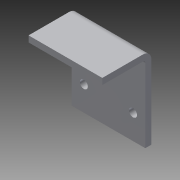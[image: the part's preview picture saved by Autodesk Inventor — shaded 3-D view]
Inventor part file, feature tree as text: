
AUTODESK INVENTOR PART (.ipt)
format: ipt  version: 2014 (Build 180170000, 170)  size: 101,376 bytes
history: native  units: in
note: dims shown in document units (in); Inventor stores cm internally (conversion verified against a paired STEP export)
features: sheet_metal_op x4, sketch x2, other x2
ambient origin geometry x8: Origin, YZ Plane, XZ Plane, XY Plane, X Axis, Y Axis, Z Axis, Center Point
bodies: Solid1 (feature_tree)
feature tree (8):
  sheet_metal_op  "Face1"
  sheet_metal_op  "Flange1"
  sketch  "Sketch1"  dims[d0=1.5in]
  other  "Plate1"
  sketch  "Sketch2"  dims[d1=1.5in d2=0.163in d3=0.25in d4=0.7874in d6=1.0in d7=0.3937in d9=1.0in d11=0.125in d12=0.125in d13=0.0625in d14=0.25in d15=0.125in d16=1.0in d17=90.0deg d18=0.05in d19=0.5in d20=0.125in d21=0.125in d22=0.5in]
  other  "Plate2"
  sheet_metal_op  "Bend1"
  sheet_metal_op  "Corner1"
